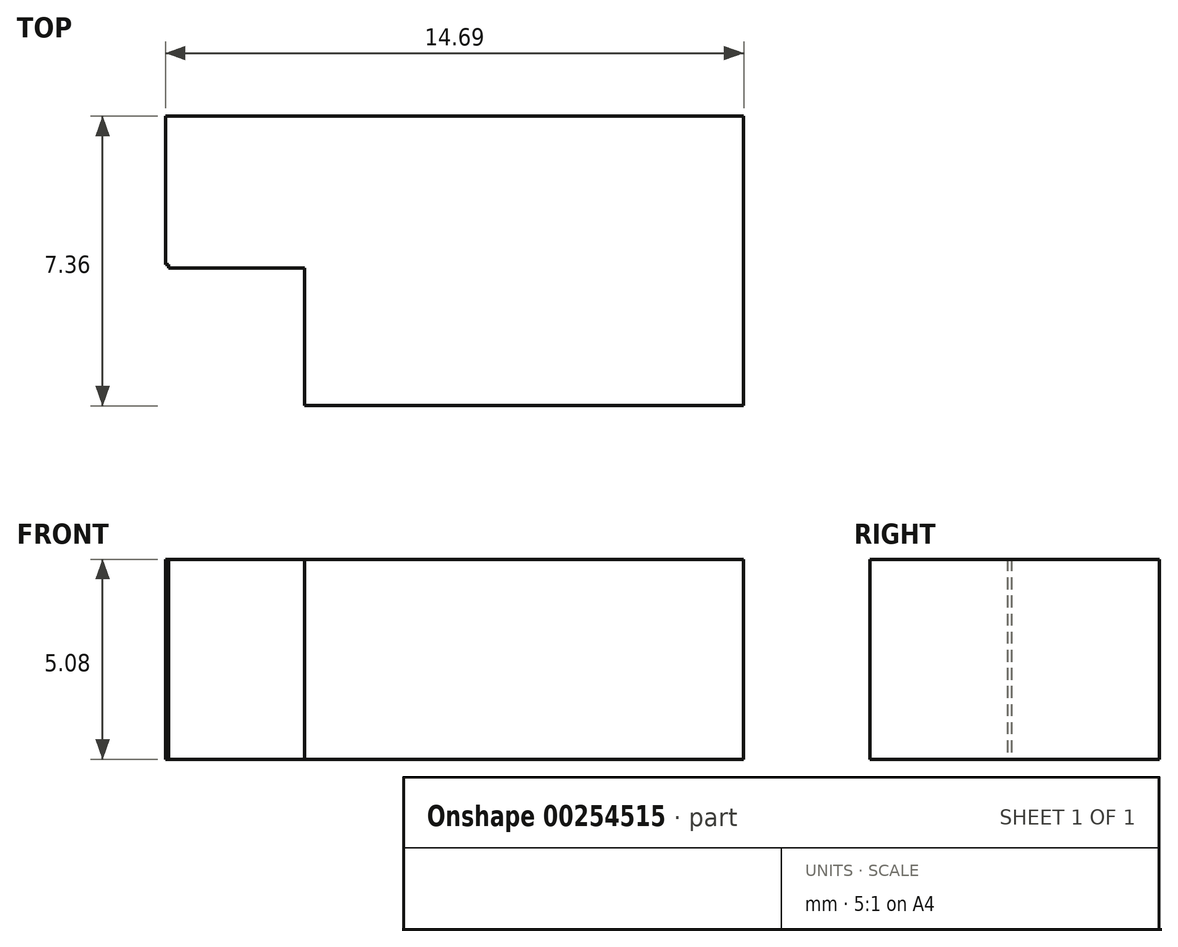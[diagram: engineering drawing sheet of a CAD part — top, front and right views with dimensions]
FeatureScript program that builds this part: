
annotation { "Feature Type Name" : "Feature", "Feature Type Description" : "" }
export const myFeature = defineFeature(function(context is Context, id is Id, definition is map)
    precondition{}
    {
        {
            var Q0;
            Q0=qCreatedBy(makeId("Top.planeOp"),FACE);
            var sketch = newSketch(context, id + "F0", { "sketchPlane" : qUnion([Q0])});
            skLineSegment(sketch, "E0", {"start": v(-33.45, 9.2) * mm, "end": v(-26.8, 16.12) * mm});
            skLineSegment(sketch, "E1", {"start": v(-26.8, 16.12) * mm, "end": v(-22.17, 16.12) * mm});
            skLineSegment(sketch, "E2", {"start": v(-22.17, 16.12) * mm, "end": v(-22.17, 19.99) * mm});
            skLineSegment(sketch, "E3", {"start": v(-22.17, 19.99) * mm, "end": v(-25.8, 19.97) * mm});
            skLineSegment(sketch, "E4", {"start": v(-25.8, 19.97) * mm, "end": v(-25.8, 38.73) * mm});
            skLineSegment(sketch, "E5", {"start": v(-25.8, 38.73) * mm, "end": v(-18.88, 45.9) * mm});
            skLineSegment(sketch, "E6", {"start": v(-18.88, 45.9) * mm, "end": v(14.3, 45.9) * mm});
            skLineSegment(sketch, "E7", {"start": v(14.3, 45.9) * mm, "end": v(22.2, 38.73) * mm});
            skLineSegment(sketch, "E8", {"start": v(22.2, 38.73) * mm, "end": v(22.2, 19.97) * mm});
            skLineSegment(sketch, "E9", {"start": v(22.2, 19.97) * mm, "end": v(18.52, 19.97) * mm});
            skLineSegment(sketch, "E10", {"start": v(18.52, 19.97) * mm, "end": v(18.52, 16.12) * mm});
            skLineSegment(sketch, "E11", {"start": v(18.52, 16.12) * mm, "end": v(22.2, 16.12) * mm});
            skLineSegment(sketch, "E12", {"start": v(22.2, 16.12) * mm, "end": v(29.83, 9.43) * mm});
            skLineSegment(sketch, "E13", {"start": v(29.83, 9.43) * mm, "end": v(29.83, -20.85) * mm});
            skLineSegment(sketch, "E14", {"start": v(29.83, -20.85) * mm, "end": v(22.14, -20.85) * mm});
            skLineSegment(sketch, "E15", {"start": v(22.14, -20.85) * mm, "end": v(22.14, -32.04) * mm});
            skLineSegment(sketch, "E16", {"start": v(22.14, -32.04) * mm, "end": v(19.03, -35.7) * mm});
            skLineSegment(sketch, "E17", {"start": v(19.03, -35.7) * mm, "end": v(3.87, -35.7) * mm});
            skLineSegment(sketch, "E18", {"start": v(3.87, -35.7) * mm, "end": v(3.87, -28.47) * mm});
            skLineSegment(sketch, "E19", {"start": v(3.87, -28.47) * mm, "end": v(-7.29, -28.47) * mm});
            skLineSegment(sketch, "E20", {"start": v(-7.29, -28.47) * mm, "end": v(-7.29, -35.7) * mm});
            skLineSegment(sketch, "E21", {"start": v(-7.29, -35.7) * mm, "end": v(-23.05, -35.7) * mm});
            skLineSegment(sketch, "E22", {"start": v(-23.05, -35.7) * mm, "end": v(-25.8, -32.44) * mm});
            skLineSegment(sketch, "E23", {"start": v(-25.8, -32.44) * mm, "end": v(-25.8, -20.85) * mm});
            skLineSegment(sketch, "E24", {"start": v(-25.8, -20.85) * mm, "end": v(-33.32, -20.85) * mm});
            skLineSegment(sketch, "E25", {"start": v(-33.32, -20.85) * mm, "end": v(-33.45, 9.2) * mm});
            skCircle(sketch, "E26", {"center": v(-11.3, 31.23) * mm, "radius": 5.9 * mm});
            skPoint(sketch, "E26.first.point", {"position": v(-17.19, 30.94) * mm});
            skPoint(sketch, "E26.second.point", {"position": v(-5.4, 31.07) * mm});
            skPoint(sketch, "E26.third.point", {"position": v(-11.26, 25.33) * mm});
            skCircle(sketch, "E27", {"center": v(7.12, 31) * mm, "radius": 5.64 * mm});
            skPoint(sketch, "E27.first.point", {"position": v(1.48, 30.84) * mm});
            skPoint(sketch, "E27.second.point", {"position": v(12.76, 30.78) * mm});
            skPoint(sketch, "E27.third.point", {"position": v(7.1, 36.64) * mm});
            skLineSegment(sketch, "E28.bottom", {"start": v(-14.96, 34.57) * mm, "end": v(-7.5, 34.57) * mm});
            skLineSegment(sketch, "E28.top", {"start": v(-14.96, 27.44) * mm, "end": v(-7.5, 27.44) * mm});
            skLineSegment(sketch, "E28.left", {"start": v(-14.96, 34.57) * mm, "end": v(-14.96, 27.44) * mm});
            skLineSegment(sketch, "E28.right", {"start": v(-7.5, 34.57) * mm, "end": v(-7.5, 27.44) * mm});
            skLineSegment(sketch, "E29.bottom", {"start": v(3.8, 34.28) * mm, "end": v(10.72, 34.28) * mm});
            skLineSegment(sketch, "E29.top", {"start": v(3.8, 27.44) * mm, "end": v(10.72, 27.44) * mm});
            skLineSegment(sketch, "E29.left", {"start": v(3.8, 34.28) * mm, "end": v(3.8, 27.44) * mm});
            skLineSegment(sketch, "E29.right", {"start": v(10.72, 34.28) * mm, "end": v(10.72, 27.44) * mm});
            skLineSegment(sketch, "E30.bottom", {"start": v(7.12, 31) * mm, "end": v(3.8, 31) * mm});
            skLineSegment(sketch, "E30.top", {"start": v(7.12, 34.28) * mm, "end": v(3.8, 34.28) * mm});
            skLineSegment(sketch, "E30.left", {"start": v(7.12, 31) * mm, "end": v(7.12, 34.28) * mm});
            skLineSegment(sketch, "E30.right", {"start": v(3.8, 31) * mm, "end": v(3.8, 34.28) * mm});
            skLineSegment(sketch, "E31.bottom", {"start": v(-11.3, 31.23) * mm, "end": v(-14.96, 31.23) * mm});
            skLineSegment(sketch, "E31.top", {"start": v(-11.3, 34.57) * mm, "end": v(-14.96, 34.57) * mm});
            skLineSegment(sketch, "E31.left", {"start": v(-11.3, 31.23) * mm, "end": v(-11.3, 34.57) * mm});
            skLineSegment(sketch, "E31.right", {"start": v(-14.96, 31.23) * mm, "end": v(-14.96, 34.57) * mm});
            skLineSegment(sketch, "E32.bottom", {"start": v(-3.8, 23.6) * mm, "end": v(0, 23.6) * mm});
            skLineSegment(sketch, "E32.top", {"start": v(-3.8, 19.8) * mm, "end": v(0, 19.8) * mm});
            skLineSegment(sketch, "E32.left", {"start": v(-3.8, 23.6) * mm, "end": v(-3.8, 19.8) * mm});
            skLineSegment(sketch, "E32.right", {"start": v(0, 23.6) * mm, "end": v(0, 19.8) * mm});
            skLineSegment(sketch, "E33.bottom", {"start": v(-7.5, 15.86) * mm, "end": v(3.8, 15.86) * mm});
            skLineSegment(sketch, "E33.top", {"start": v(-7.5, 12.27) * mm, "end": v(3.8, 12.27) * mm});
            skLineSegment(sketch, "E33.left", {"start": v(-7.5, 15.86) * mm, "end": v(-7.5, 12.27) * mm});
            skLineSegment(sketch, "E33.right", {"start": v(3.8, 15.86) * mm, "end": v(3.8, 12.27) * mm});
            skPoint(sketch, "E34.oppositeSnap0", {"position": v(-25.8, -26.64) * mm});
            skLineSegment(sketch, "E34.bottom", {"start": v(-29.45, -9.9) * mm, "end": v(-25.8, -9.9) * mm});
            skLineSegment(sketch, "E34.top", {"start": v(-29.45, -17.27) * mm, "end": v(-25.8, -17.27) * mm});
            skLineSegment(sketch, "E34.left", {"start": v(-29.45, -9.9) * mm, "end": v(-29.45, -17.27) * mm});
            skLineSegment(sketch, "E34.right", {"start": v(-25.8, -9.9) * mm, "end": v(-25.8, -17.27) * mm});
            skLineSegment(sketch, "E35.top", {"start": v(-29.45, 8.74) * mm, "end": v(-25.8, 8.74) * mm});
            skLineSegment(sketch, "E35.left", {"start": v(-29.45, -9.9) * mm, "end": v(-29.45, 8.74) * mm});
            skLineSegment(sketch, "E35.right", {"start": v(-25.8, -9.9) * mm, "end": v(-25.8, 8.74) * mm});
            skLineSegment(sketch, "E36.bottom", {"start": v(22.2, -9.9) * mm, "end": v(25.76, -9.9) * mm});
            skLineSegment(sketch, "E36.top", {"start": v(22.2, -17.27) * mm, "end": v(25.76, -17.27) * mm});
            skLineSegment(sketch, "E36.left", {"start": v(22.2, -9.9) * mm, "end": v(22.2, -17.27) * mm});
            skLineSegment(sketch, "E36.right", {"start": v(25.76, -9.9) * mm, "end": v(25.76, -17.27) * mm});
            skLineSegment(sketch, "E37.top", {"start": v(22.2, 8.7) * mm, "end": v(25.76, 8.7) * mm});
            skLineSegment(sketch, "E37.left", {"start": v(22.2, -9.9) * mm, "end": v(22.2, 8.7) * mm});
            skLineSegment(sketch, "E37.right", {"start": v(25.76, -9.9) * mm, "end": v(25.76, 8.7) * mm});
            skLineSegment(sketch, "E38.bottom", {"start": v(-3.6, -28.47) * mm, "end": v(0, -28.47) * mm});
            skLineSegment(sketch, "E38.top", {"start": v(-3.6, -24.74) * mm, "end": v(0, -24.74) * mm});
            skLineSegment(sketch, "E38.left", {"start": v(-3.6, -28.47) * mm, "end": v(-3.6, -24.74) * mm});
            skLineSegment(sketch, "E38.right", {"start": v(0, -28.47) * mm, "end": v(0, -24.74) * mm});
            skLineSegment(sketch, "E39", {"start": v(-22.24, -24.61) * mm, "end": v(-22.24, -31.85) * mm});
            skLineSegment(sketch, "E40", {"start": v(-22.24, -31.85) * mm, "end": v(-11.06, -31.85) * mm});
            skLineSegment(sketch, "E41", {"start": v(-11.06, -31.85) * mm, "end": v(-11.06, -28.48) * mm});
            skLineSegment(sketch, "E42", {"start": v(-11.06, -28.48) * mm, "end": v(-7.29, -28.47) * mm});
            skLineSegment(sketch, "E43", {"start": v(-7.29, -24.61) * mm, "end": v(-22.24, -24.61) * mm});
            skLineSegment(sketch, "E44", {"start": v(-7.29, -24.61) * mm, "end": v(-7.29, -28.47) * mm});
            skLineSegment(sketch, "E45", {"start": v(3.87, -28.47) * mm, "end": v(3.87, -24.61) * mm});
            skLineSegment(sketch, "E46", {"start": v(3.87, -24.61) * mm, "end": v(18.56, -24.61) * mm});
            skLineSegment(sketch, "E47", {"start": v(18.56, -24.61) * mm, "end": v(18.56, -31.97) * mm});
            skLineSegment(sketch, "E48", {"start": v(18.56, -31.97) * mm, "end": v(7.4, -31.97) * mm});
            skLineSegment(sketch, "E49", {"start": v(7.4, -31.97) * mm, "end": v(7.4, -28.47) * mm});
            skLineSegment(sketch, "E50", {"start": v(7.4, -28.47) * mm, "end": v(3.87, -28.47) * mm});
            skLineSegment(sketch, "E51", {"start": v(-22.17, 19.99) * mm, "end": v(-22.24, 38.23) * mm});
            skLineSegment(sketch, "E52", {"start": v(-22.24, 38.23) * mm, "end": v(-18.48, 38.25) * mm});
            skLineSegment(sketch, "E53", {"start": v(-18.48, 38.25) * mm, "end": v(-18.5, 42.04) * mm});
            skLineSegment(sketch, "E54", {"start": v(-18.5, 42.04) * mm, "end": v(14.76, 42.16) * mm});
            skLineSegment(sketch, "E55", {"start": v(14.76, 42.16) * mm, "end": v(14.78, 38.23) * mm});
            skLineSegment(sketch, "E56", {"start": v(14.78, 38.23) * mm, "end": v(18.52, 38.24) * mm});
            skLineSegment(sketch, "E57", {"start": v(18.52, 38.24) * mm, "end": v(18.52, 19.97) * mm});
            skLineSegment(sketch, "E58", {"start": v(3.8, 15.86) * mm, "end": v(3.8, 19.97) * mm});
            skLineSegment(sketch, "E59", {"start": v(3.8, 19.97) * mm, "end": v(18.52, 19.97) * mm});
            skLineSegment(sketch, "E60", {"start": v(-7.5, 15.86) * mm, "end": v(-7.5, 19.99) * mm});
            skLineSegment(sketch, "E61", {"start": v(-7.5, 19.99) * mm, "end": v(-22.17, 19.99) * mm});
            skLineSegment(sketch, "E62", {"start": v(-22.23, 12.38) * mm, "end": v(-22.23, -21.38) * mm});
            skLineSegment(sketch, "E63", {"start": v(-22.23, -21.38) * mm, "end": v(18.48, -21.38) * mm});
            skLineSegment(sketch, "E64", {"start": v(18.48, -21.38) * mm, "end": v(18.48, 12.34) * mm});
            skLineSegment(sketch, "E65", {"start": v(18.48, 12.34) * mm, "end": v(14.65, 12.34) * mm});
            skLineSegment(sketch, "E66", {"start": v(14.65, 12.34) * mm, "end": v(14.65, 15.86) * mm});
            skLineSegment(sketch, "E67", {"start": v(14.65, 15.86) * mm, "end": v(3.8, 15.86) * mm});
            skLineSegment(sketch, "E68", {"start": v(-22.23, 12.38) * mm, "end": v(-18.53, 12.38) * mm});
            skLineSegment(sketch, "E69", {"start": v(-18.53, 12.38) * mm, "end": v(-18.53, 15.86) * mm});
            skLineSegment(sketch, "E70", {"start": v(-18.53, 15.86) * mm, "end": v(-7.5, 15.86) * mm});
            skLineSegment(sketch, "E71.bottom", {"start": v(-7.42, -28.31) * mm, "end": v(-7.13, -28.31) * mm});
            skLineSegment(sketch, "E71.top", {"start": v(-7.42, -28.63) * mm, "end": v(-7.13, -28.63) * mm});
            skLineSegment(sketch, "E71.left", {"start": v(-7.42, -28.31) * mm, "end": v(-7.42, -28.63) * mm});
            skLineSegment(sketch, "E71.right", {"start": v(-7.13, -28.31) * mm, "end": v(-7.13, -28.63) * mm});
            skLineSegment(sketch, "E72.bottom", {"start": v(3.95, -28.38) * mm, "end": v(3.78, -28.38) * mm});
            skLineSegment(sketch, "E72.top", {"start": v(3.95, -28.56) * mm, "end": v(3.78, -28.56) * mm});
            skLineSegment(sketch, "E72.left", {"start": v(3.95, -28.38) * mm, "end": v(3.95, -28.56) * mm});
            skLineSegment(sketch, "E72.right", {"start": v(3.78, -28.38) * mm, "end": v(3.78, -28.56) * mm});
            skSolve(sketch);
        }
        {
            var Q0;
            {var subQ0=sQuery(id+"F0.wireOp",EDGE,"E46");Q0=makeQuery(id+"F0.imprint","IMPRINT",FACE,{"disambiguationData":[TD([[makeQuery(id+"F0.imprint","IMPRINT",EDGE,{"derivedFrom":subQ0}),-1.0]])]});}
            extrude(context, id + "F1", {"entities" : qUnion([Q0]), "depth" : 5.08 * mm});
        }
    });
